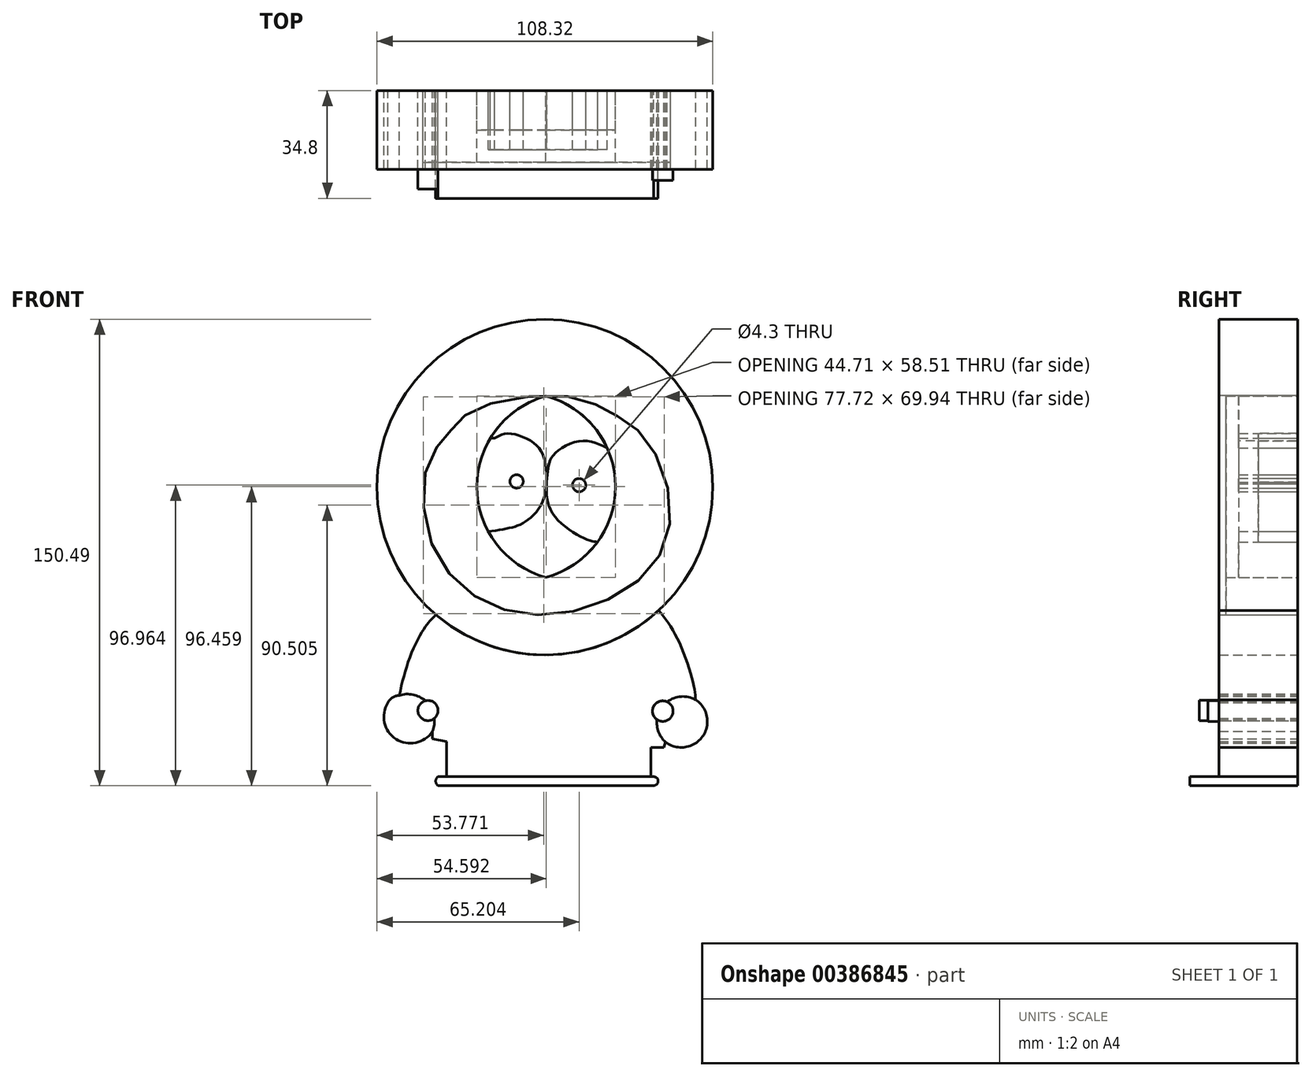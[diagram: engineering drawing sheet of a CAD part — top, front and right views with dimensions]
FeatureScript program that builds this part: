
annotation { "Feature Type Name" : "Feature", "Feature Type Description" : "" }
export const myFeature = defineFeature(function(context is Context, id is Id, definition is map)
    precondition{}
    {
        {
            var Q0;
            Q0=qCreatedBy(makeId("Front.planeOp"),FACE);
            var sketch = newSketch(context, id + "F0", { "sketchPlane" : qUnion([Q0])});
            skCircle(sketch, "E0", {"center": v(-0.3, 21.13) * mm, "radius": 54.16 * mm});
            skPoint(sketch, "E1.center.orphan", {"position": v(0, 11.8) * mm});
            skArc(sketch, "E2", {"start": v(0, -8) * mm, "mid": v(22.5, 21.26) * mm, "end": v(0, 50.52) * mm});
            skArc(sketch, "E3", {"start": v(0, 50.52) * mm, "mid": v(-22.21, 21.26) * mm, "end": v(0, -8) * mm});
            skFitSpline(sketch, "E4", {"points": [v(-30.44, 39.58) * mm, v(-37.83, 29.24) * mm, v(-36.94, 3.23) * mm, v(-20.69, -15.39) * mm, v(3.25, -19.82) * mm, v(29.26, -9.48) * mm, v(40.2, 10.62) * mm, v(32.8, 36.03) * mm, v(21.57, 44.9) * mm, v(6.2, 50.52) * mm, v(-23.35, 46.08) * mm, v(-30.44, 39.58) * mm]});
            skLineSegment(sketch, "E5", {"start": v(0, -37.25) * mm, "end": v(0, -64.74) * mm});
            skLineSegment(sketch, "E6", {"start": v(-34.79, -72.33) * mm, "end": v(34.83, -72.33) * mm});
            skLineSegment(sketch, "E7", {"start": v(-34.79, -75.2) * mm, "end": v(34.81, -75.2) * mm});
            skArc(sketch, "E8", {"start": v(34.81, -75.2) * mm, "mid": v(36.24, -73.77) * mm, "end": v(34.83, -72.33) * mm});
            skArc(sketch, "E9", {"start": v(-34.79, -72.33) * mm, "mid": v(-35.51, -73.76) * mm, "end": v(-34.79, -75.2) * mm});
            skLineSegment(sketch, "E10", {"start": v(-32.03, -60.98) * mm, "end": v(-32.03, -72.33) * mm});
            skLineSegment(sketch, "E11", {"start": v(-32.03, -60.98) * mm, "end": v(-36.57, -60.04) * mm});
            skLineSegment(sketch, "E12", {"start": v(-36.57, -60.04) * mm, "end": v(-36.57, -57.71) * mm});
            skArc(sketch, "E13", {"start": v(-50.93, -48.46) * mm, "mid": v(-48.33, -60.18) * mm, "end": v(-36.57, -57.71) * mm});
            skArc(sketch, "E14", {"start": v(-47.28, -46.1) * mm, "mid": v(-49.44, -46.76) * mm, "end": v(-50.93, -48.46) * mm});
            skFitSpline(sketch, "E15", {"points": [v(-47.28, -46.1) * mm, v(-43.78, -33.6) * mm, v(-39.19, -24.42) * mm, v(-37.25, -21.98) * mm, v(-35.42, -20.09) * mm], "startDerivative": vector(8.2, 35.74) * mm, "endDerivative": vector(11.83, 12.07) * mm});
            skCircle(sketch, "E16", {"center": v(-38, -50.96) * mm, "radius": 3.25 * mm});
            skCircle(sketch, "E17", {"center": v(37.74, -51.16) * mm, "radius": 3.32 * mm});
            skLineSegment(sketch, "E18", {"start": v(33.88, -62.95) * mm, "end": v(33.88, -72.33) * mm});
            skLineSegment(sketch, "E19", {"start": v(33.88, -62.95) * mm, "end": v(38.05, -62.95) * mm});
            skLineSegment(sketch, "E20", {"start": v(38.05, -62.95) * mm, "end": v(38.6, -61.15) * mm});
            skArc(sketch, "E21", {"start": v(38.6, -61.15) * mm, "mid": v(50.56, -59.37) * mm, "end": v(48.35, -47.49) * mm});
            skArc(sketch, "E22", {"start": v(48.35, -47.49) * mm, "mid": v(43.65, -46.46) * mm, "end": v(39.16, -48.16) * mm});
            skArc(sketch, "E23.trimOffspring", {"start": v(35.88, -53.9) * mm, "mid": v(36.36, -57.86) * mm, "end": v(38.6, -61.15) * mm});
            skArc(sketch, "E24", {"start": v(-36.57, -57.71) * mm, "mid": v(-36, -55.64) * mm, "end": v(-35.94, -53.48) * mm});
            skArc(sketch, "E25.trimOffspring", {"start": v(-38.86, -47.82) * mm, "mid": v(-42.84, -45.85) * mm, "end": v(-47.28, -46.1) * mm});
            skLineSegment(sketch, "E26", {"start": v(-33.08, -41.88) * mm, "end": v(-35.05, -49.6) * mm});
            skCircle(sketch, "E27", {"center": v(-9.44, 22.96) * mm, "radius": 2.15 * mm});
            skCircle(sketch, "E28", {"center": v(10.75, 21.76) * mm, "radius": 2.15 * mm});
            skFitSpline(sketch, "E29", {"points": [v(-16.57, 36.9) * mm, v(-11.97, 38.43) * mm, v(-3.24, 34.83) * mm, v(0, 28.03) * mm, v(-1.04, 16.37) * mm, v(-6.7, 9.9) * mm, v(-11.3, 8.03) * mm, v(-18.55, 6.8) * mm], "startDerivative": vector(35.29, 20.38) * mm, "endDerivative": vector(-55.14, -7.9) * mm});
            skFitSpline(sketch, "E30", {"points": [v(19.77, 33.81) * mm, v(11.29, 36.03) * mm, v(2.89, 31.96) * mm, v(0.96, 28.23) * mm, v(0.27, 22.76) * mm, v(2.22, 12.63) * mm, v(13.42, 4.17) * mm, v(16.7, 3.45) * mm], "startDerivative": vector(-52.9, 24.4) * mm, "endDerivative": vector(28, -2) * mm});
            skLineSegment(sketch, "E31", {"start": v(-16.57, 36.9) * mm, "end": v(-17.88, 36.9) * mm});
            skFitSpline(sketch, "E32", {"points": [v(36.44, -18.67) * mm, v(42.35, -27.56) * mm, v(47.63, -42.55) * mm, v(48.35, -47.49) * mm], "startDerivative": vector(17.63, -22.31) * mm, "endDerivative": vector(1.43, -17.56) * mm});
            skSolve(sketch);
        }
        {
            var Q0;
            Q0=makeQuery(id+"F0.imprint","IMPRINT",FACE,{"disambiguationData":[TD([[makeQuery(id+"F0.imprint","IMPRINT",EDGE,{"derivedFrom":sQuery(id+"F0.wireOp",EDGE,"E13")}),1.0]])]});
            var Q1;
            Q1=makeQuery(id+"F0.imprint","IMPRINT",FACE,{"disambiguationData":[TD([[makeQuery(id+"F0.imprint","IMPRINT",EDGE,{"derivedFrom":sQuery(id+"F0.wireOp",EDGE,"E21")}),1.0]])]});
            var Q2;
            Q2=makeQuery(id+"F0.imprint","IMPRINT",FACE,{"disambiguationData":[TD([[makeQuery(id+"F0.imprint","IMPRINT",EDGE,{"derivedFrom":sQuery(id+"F0.wireOp",EDGE,"E0")}),1.0]])]});
            extrude(context, id + "F1", {"entities" : qUnion([Q0, Q1, Q2]), "depth" : 25.4 * mm});
        }
        {
            var Q0;
            {var subQ7=sQuery(id+"F0.wireOp",EDGE,"E31");Q0=makeQuery(id+"F0.imprint","IMPRINT",FACE,{"disambiguationData":[TD([[makeQuery(id+"F0.imprint","IMPRINT",EDGE,{"derivedFrom":subQ7}),-1.0]])]});}
            var Q1;
            {var subQ0=sQuery(id+"F0.wireOp",EDGE,"E3");var subQ1=sQuery(id+"F0.wireOp",EDGE,"E2");var subQ2=makeQuery(id+"F0.imprint","INTERSECT",VERTEX,{"disambiguationData":[OD(0.0)],"derivedFrom":[subQ1,subQ0]});Q1=makeQuery(id+"F0.imprint","IMPRINT",FACE,{"disambiguationData":[TD([[makeQuery(id+"F0.imprint","IMPRINT",EDGE,{"disambiguationData":[TD([[subQ2,-1.0]])],"derivedFrom":subQ1}),1.0]])]});}
            var Q2;
            Q2=makeQuery(id+"F0.imprint","IMPRINT",FACE,{"disambiguationData":[TD([[makeQuery(id+"F0.imprint","IMPRINT",EDGE,{"derivedFrom":sQuery(id+"F0.wireOp",EDGE,"E27")}),1.0]])]});
            var Q3;
            Q3=makeQuery(id+"F0.imprint","IMPRINT",FACE,{"disambiguationData":[TD([[makeQuery(id+"F0.imprint","IMPRINT",EDGE,{"derivedFrom":sQuery(id+"F0.wireOp",EDGE,"E28")}),1.0]])]});
            extrude(context, id + "F2", {"entities" : qUnion([Q0, Q1, Q2, Q3]), "depth" : 19.05 * mm});
        }
        {
            var Q0;
            Q0=makeQuery(id+"F0.imprint","IMPRINT",FACE,{"disambiguationData":[TD([[makeQuery(id+"F0.imprint","IMPRINT",EDGE,{"derivedFrom":sQuery(id+"F0.wireOp",EDGE,"E27")}),-1.0]])]});
            var Q1;
            Q1=makeQuery(id+"F0.imprint","IMPRINT",FACE,{"disambiguationData":[TD([[makeQuery(id+"F0.imprint","IMPRINT",EDGE,{"derivedFrom":sQuery(id+"F0.wireOp",EDGE,"E28")}),-1.0]])]});
            extrude(context, id + "F3", {"entities" : qUnion([Q0, Q1]), "depth" : 12.7 * mm});
        }
        {
            var Q0;
            Q0=makeQuery(id+"F0.imprint","IMPRINT",FACE,{"disambiguationData":[TD([[makeQuery(id+"F0.imprint","IMPRINT",EDGE,{"derivedFrom":sQuery(id+"F0.wireOp",EDGE,"E4")}),1.0]])]});
            extrude(context, id + "F4", {"entities" : qUnion([Q0]), "depth" : 23.1 * mm});
        }
        {
            var Q0;
            {var subQ0=sQuery(id+"F0.wireOp",EDGE,"E17");var subQ1=makeQuery(id+"F0.imprint","INTERSECT",VERTEX,{"derivedFrom":[subQ0,sQuery(id+"F0.wireOp",EDGE,"E22")]});Q0=makeQuery(id+"F0.imprint","IMPRINT",FACE,{"disambiguationData":[TD([[makeQuery(id+"F0.imprint","IMPRINT",EDGE,{"disambiguationData":[TD([[subQ1,-1.0]])],"derivedFrom":subQ0}),1.0]])]});}
            extrude(context, id + "F5", {"entities" : qUnion([Q0]), "operationType" : NewBodyOperationType.ADD, "depth" : 28.96 * mm});
        }
        {
            var Q0;
            Q0=makeQuery(id+"F0.imprint","IMPRINT",FACE,{"disambiguationData":[TD([[makeQuery(id+"F0.imprint","IMPRINT",EDGE,{"derivedFrom":sQuery(id+"F0.wireOp",EDGE,"E7")}),1.0]])]});
            extrude(context, id + "F6", {"entities" : qUnion([Q0]), "depth" : 34.8 * mm});
        }
        {
            var Q0;
            {var subQ10=sQuery(id+"F0.wireOp",EDGE,"E10");Q0=makeQuery(id+"F0.imprint","IMPRINT",FACE,{"disambiguationData":[TD([[makeQuery(id+"F0.imprint","IMPRINT",EDGE,{"derivedFrom":subQ10}),1.0]])]});}
            extrude(context, id + "F7", {"entities" : qUnion([Q0]), "depth" : 25.4 * mm});
        }
        {
            var Q0;
            {var subQ0=sQuery(id+"F0.wireOp",EDGE,"E16");var subQ2=makeQuery(id+"F0.imprint","IMPRINT",VERTEX,{"derivedFrom":subQ0});Q0=makeQuery(id+"F0.imprint","IMPRINT",FACE,{"disambiguationData":[TD([[makeQuery(id+"F0.imprint","IMPRINT",EDGE,{"disambiguationData":[TD([[subQ2,-1.0]])],"derivedFrom":subQ0}),1.0]])]});}
            extrude(context, id + "F8", {"entities" : qUnion([Q0]), "depth" : 31.75 * mm});
        }
    });
